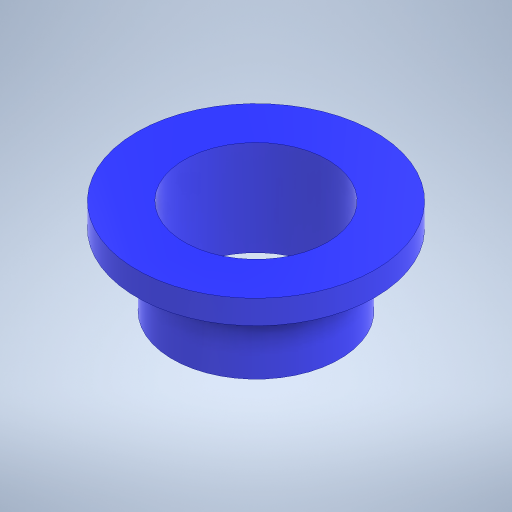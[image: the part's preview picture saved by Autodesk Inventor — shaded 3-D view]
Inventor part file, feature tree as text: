
AUTODESK INVENTOR PART (.ipt)
format: ipt  version: 2024 (Build 280153000, 153)  size: 241,152 bytes
history: native  units: mm
features: extrude x2, sketch x1
ambient origin geometry x8: Origin, YZ Plane, XZ Plane, XY Plane, X Axis, Y Axis, Z Axis, Center Point
bodies: Solid1 (feature_tree)
feature tree (3):
  extrude  "Extrusion1"  Depth=1.0mm
  extrude  "Extrusion2"  Depth=3.0mm TaperAngle=0.0deg
  sketch  "Sketch2"  dims[d0=6.0mm d1=7.0mm d2=3.0mm d3=0.0mm d4=13.0mm d5=1.0mm d6=0.0mm]
